# Revit family: OASIS TS-6030 STD
name_source: partatom
category: Plumbing Fixtures
units: mm (PartAtom-declared; Revit-internal decimal feet)

## family parameters
Always vertical = Yes
Cut with Voids When Loaded = No
OmniClass Number = 23.45.05.14.21.11
OmniClass Title = Bath/Shower Units
Part Type = Normal
Room Calculation Point = No
Round Connector Dimension = Use Diameter
Shared = No
Work Plane-Based = No

## types (5) — shared parameters
BIM Model By = www.shive-hattery.com
Cold Water Connector = Cold Water Connection
Color = <By Category>
Default Elevation = 0"
Grab Bar Finish = <By Category>
Hot Water Connector = Hot Water Connection
Manufacturer = OASIS
Sanitary Connector = Sanitary Connection
Seat Finish = <By Category>
Shower Rod = No
Stainless steel = <By Category>
Type Comments = Combination Tub & Shower
URL = www.oasisbath.com

## per-type parameters (varying)
| type | Bar_Horz_Back_High | Bar_Horz_Back_Low | Bar_Horz_Left | Bar_Horz_Right | Bar_Vert | Model |
| BP1-60 Package | Yes | No | Yes | No | No | TS-6030 STD/BP1-60 |
| Base Model, 3SF, 3SM, & FH Packages | No | No | No | No | No | TS-6030 STD/(Base Model,3SF,3SM,FH) |
| BP2-60 Package | Yes | No | Yes | No | Yes | TS-6030 STD/BP2-60 |
| 4BAR Package | Yes | Yes | Yes | Yes | No | TS-6030 STD/4BAR |
| 5BAR Package | Yes | Yes | Yes | Yes | Yes | TS-6030 STD/5BAR |

## geometry (parser evidence)
native form markers: Blend x4, Sweep x3
no freeform markers — native parametric forms only
